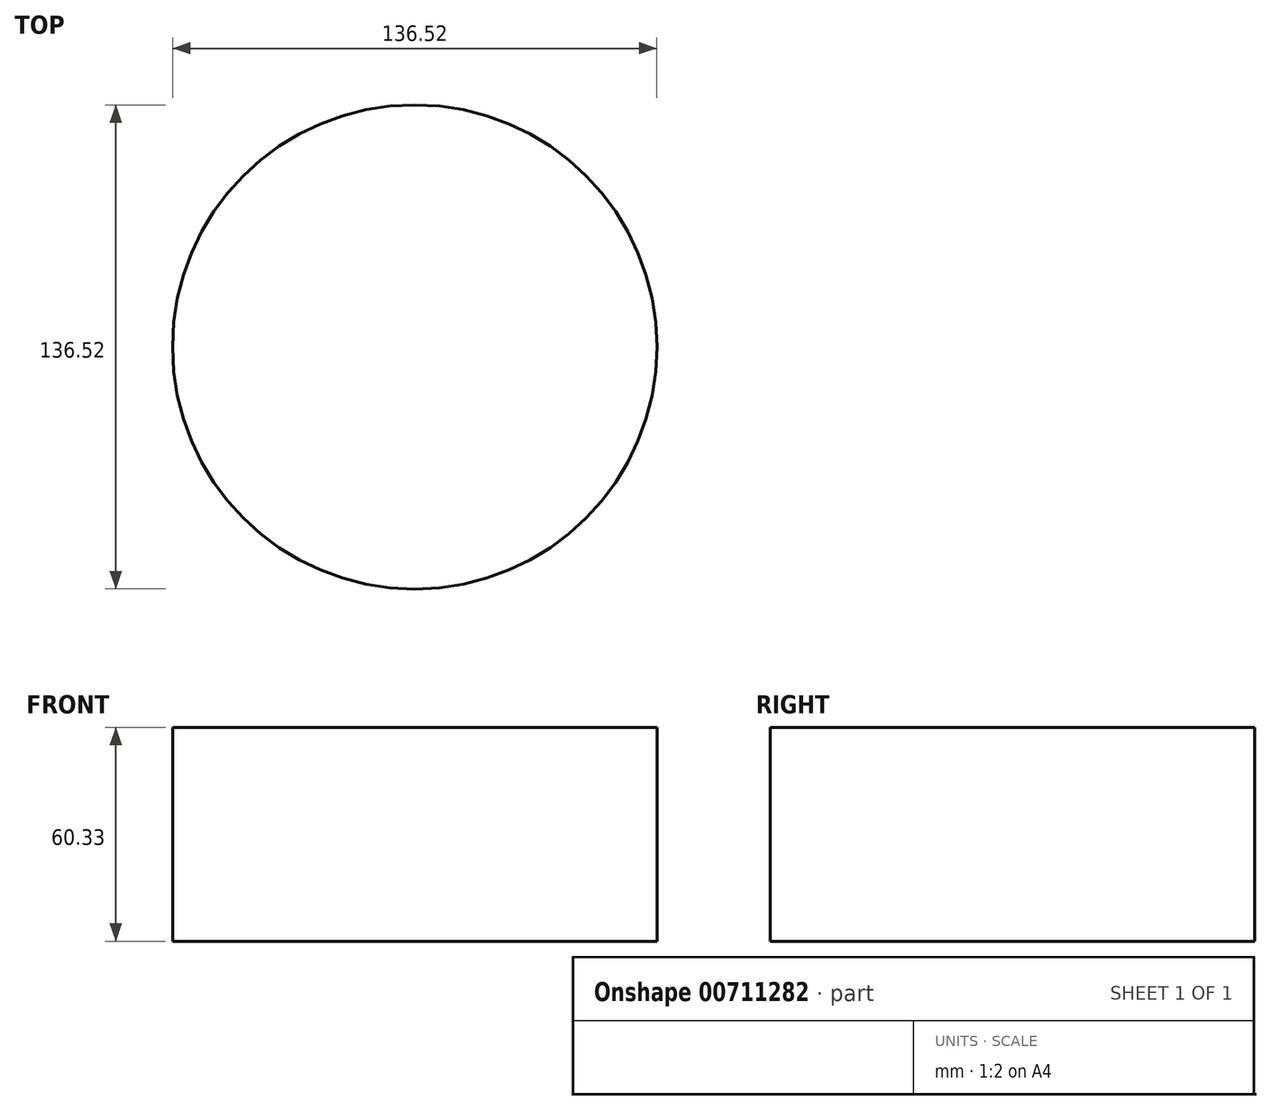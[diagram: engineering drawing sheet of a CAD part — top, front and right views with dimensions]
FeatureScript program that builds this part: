
annotation { "Feature Type Name" : "Feature", "Feature Type Description" : "" }
export const myFeature = defineFeature(function(context is Context, id is Id, definition is map)
    precondition{}
    {
        {
            var Q0;
            Q0=qCreatedBy(makeId("Top.planeOp"),FACE);
            var sketch = newSketch(context, id + "F0", { "sketchPlane" : qUnion([Q0])});
            skCircle(sketch, "E0", {"center": v(53.1, -46.15) * mm, "radius": 68.26 * mm});
            skSolve(sketch);
        }
        {
            var Q0;
            Q0=makeQuery(id+"F0.imprint","IMPRINT",FACE,{"disambiguationData":[TD([[makeQuery(id+"F0.imprint","IMPRINT",EDGE,{"derivedFrom":sQuery(id+"F0.wireOp",EDGE,"E0")}),1.0]])]});
            extrude(context, id + "F1", {"entities" : qUnion([Q0]), "depth" : 60.32 * mm, "offsetDistance" : 25.4 * mm});
        }
    });
